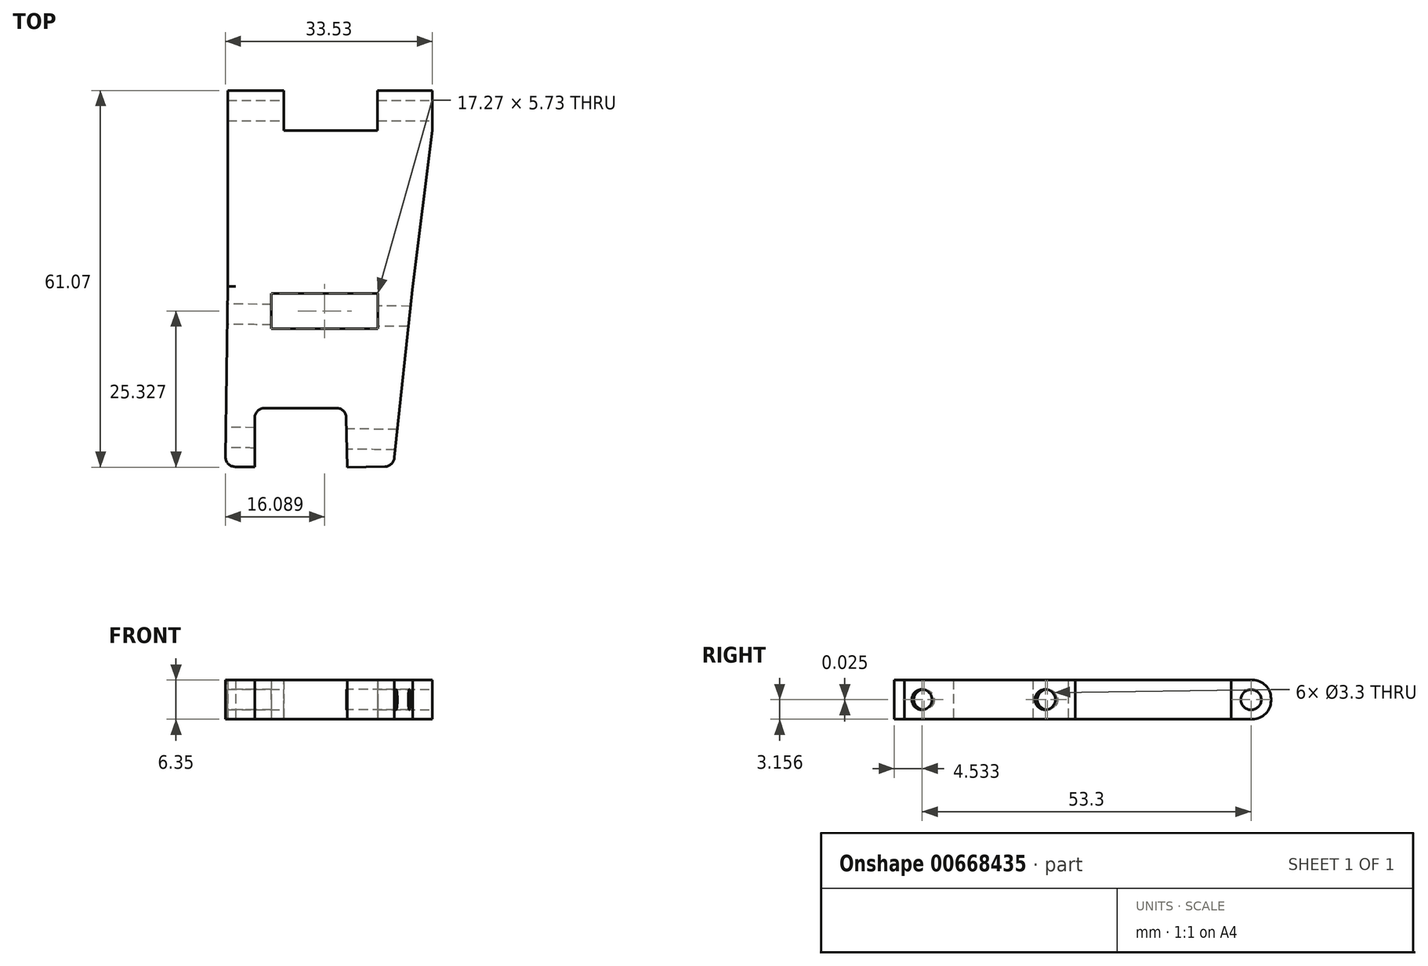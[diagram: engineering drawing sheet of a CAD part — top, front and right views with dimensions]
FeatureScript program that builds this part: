
annotation { "Feature Type Name" : "Feature", "Feature Type Description" : "" }
export const myFeature = defineFeature(function(context is Context, id is Id, definition is map)
    precondition{}
    {
        {
            var Q0;
            Q0=qCreatedBy(makeId("Top.planeOp"),FACE);
            var sketch = newSketch(context, id + "F0", { "sketchPlane" : qUnion([Q0])});
            skLineSegment(sketch, "E0.bottom", {"start": v(-49.27, 51.46) * mm, "end": v(-40.15, 51.46) * mm});
            skLineSegment(sketch, "E0.top", {"start": v(-49.27, 19.7) * mm, "end": v(-19.3, 19.7) * mm});
            skLineSegment(sketch, "E0.left", {"start": v(-49.27, 51.46) * mm, "end": v(-49.27, 19.7) * mm});
            skLineSegment(sketch, "E0.right", {"start": v(-16.1, 51.46) * mm, "end": v(-16.1, 45.01) * mm});
            skLineSegment(sketch, "E1", {"start": v(-40.15, 51.46) * mm, "end": v(-40.15, 45.01) * mm});
            skLineSegment(sketch, "E2", {"start": v(-40.15, 45.01) * mm, "end": v(-25, 45.01) * mm});
            skLineSegment(sketch, "E3", {"start": v(-25, 45.01) * mm, "end": v(-25, 51.46) * mm});
            skLineSegment(sketch, "E4", {"start": v(-25, 51.46) * mm, "end": v(-16.1, 51.46) * mm});
            skLineSegment(sketch, "E5", {"start": v(-16.1, 45.01) * mm, "end": v(-19.3, 19.7) * mm});
            skSolve(sketch);
        }
        {
            var Q0;
            Q0=makeQuery(id+"F0.imprint","IMPRINT",FACE,{"disambiguationData":[TD([[makeQuery(id+"F0.imprint","IMPRINT",EDGE,{"derivedFrom":sQuery(id+"F0.wireOp",EDGE,"E0.top")}),1.0]])]});
            extrude(context, id + "F1", {"entities" : qUnion([Q0]), "depth" : 6.35 * mm});
        }
        {
            var Q0;
            Q0=makeQuery(id+"F1.opExtrude","SWEPT_FACE",FACE,{"disambiguationData":[OSD([sQuery(id+"F0.wireOp",EDGE,"E0.right")])]});
            var sketch = newSketch(context, id + "F2", { "sketchPlane" : qUnion([Q0])});
            skCircle(sketch, "E6", {"center": v(48.22, 3.16) * mm, "radius": 1.5 * mm});
            skSolve(sketch);
        }
        {
            var Q0;
            Q0=sQuery(id+"F2.wireOp",VERTEX,"E6.center");
            var Q1;
            Q1=makeQuery(id+"F1.opExtrude","SWEPT_BODY",BODY,{"disambiguationData":[OSD([sQuery(id+"F0.wireOp",EDGE,"E0.top"),sQuery(id+"F0.wireOp",EDGE,"E0.left"),sQuery(id+"F0.wireOp",EDGE,"E0.bottom"),sQuery(id+"F0.wireOp",EDGE,"E1"),sQuery(id+"F0.wireOp",EDGE,"E2"),sQuery(id+"F0.wireOp",EDGE,"E3"),sQuery(id+"F0.wireOp",EDGE,"E0.right"),sQuery(id+"F0.wireOp",EDGE,"E5"),sQuery(id+"F0.wireOp",EDGE,"E4")])]});
            hole(context, id + "F3", {"style" : HoleStyle.SIMPLE, "endStyle" : HoleEndStyle.THROUGH, "standardTappedOrClearance" : lookupTablePath({ "standard" : "ISO", "fit" : "Normal", "size" : "M3", "type" : "Clearance" }), "standardBlindInLast" : lookupTablePath({ "fit" : "Standard", "standard" : "ISO", "size" : "M3", "type" : "Clearance" }), "holeDiameter" : 3.3 * mm, "isTappedThrough" : true, "tappedDepth" : 12.7 * mm, "tapClearance" : 3, "locations" : qUnion([Q0]), "scope" : qUnion([Q1])});
        }
        {
            var Q0;
            Q0=makeQuery(id+"F1.opExtrude","CAP_EDGE",EDGE,{"disambiguationData":[OSD([sQuery(id+"F0.wireOp",EDGE,"E4")])],"isStart":true});
            var Q1;
            Q1=makeQuery(id+"F1.opExtrude","CAP_EDGE",EDGE,{"disambiguationData":[OSD([sQuery(id+"F0.wireOp",EDGE,"E4")])],"isStart":false});
            var Q2;
            Q2=makeQuery(id+"F1.opExtrude","CAP_EDGE",EDGE,{"disambiguationData":[OSD([sQuery(id+"F0.wireOp",EDGE,"E0.bottom")])],"isStart":true});
            var Q3;
            Q3=makeQuery(id+"F1.opExtrude","CAP_EDGE",EDGE,{"disambiguationData":[OSD([sQuery(id+"F0.wireOp",EDGE,"E0.bottom")])],"isStart":false});
            fillet(context, id + "F4", {"entities" : qUnion([Q0, Q1, Q2, Q3]), "radius" : 3 * mm, "tangentPropagation" : true, "allowEdgeOverflow" : false});
        }
        {
            var Q0;
            Q0=qCreatedBy(makeId("Top.planeOp"),FACE);
            var sketch = newSketch(context, id + "F5", { "sketchPlane" : qUnion([Q0])});
            skLineSegment(sketch, "E7", {"start": v(-49.63, 0) * mm, "end": v(-49.63, -7.95) * mm});
            skLineSegment(sketch, "E8", {"start": v(-44.88, -9.53) * mm, "end": v(-44.88, -1.59) * mm});
            skLineSegment(sketch, "E9", {"start": v(-48.05, -9.53) * mm, "end": v(-44.88, -9.53) * mm});
            skLineSegment(sketch, "E10", {"start": v(-29.9, -9.61) * mm, "end": v(-23.8, -9.5) * mm});
            skLineSegment(sketch, "E11", {"start": v(-43.29, 0) * mm, "end": v(-31.63, 0) * mm});
            skPoint(sketch, "E12.visualSharp", {"position": v(-26.3, 0) * mm});
            skPoint(sketch, "E13.visualSharp", {"position": v(-44.88, 0) * mm});
            skArc(sketch, "E13.filletArc", {"start": v(-43.29, 0) * mm, "mid": v(-44.41, -0.46) * mm, "end": v(-44.88, -1.59) * mm});
            skPoint(sketch, "E14.visualSharp", {"position": v(-49.63, -9.53) * mm});
            skArc(sketch, "E14.filletArc", {"start": v(-49.63, -7.95) * mm, "mid": v(-49.16, -9.06) * mm, "end": v(-48.05, -9.53) * mm});
            skPoint(sketch, "E15.visualSharp", {"position": v(-25.16, -9.53) * mm});
            skArc(sketch, "E15.filletArc", {"start": v(-23.8, -9.5) * mm, "mid": v(-22.7, -9.04) * mm, "end": v(-22.25, -7.95) * mm});
            skLineSegment(sketch, "E16", {"start": v(-19.3, 19.74) * mm, "end": v(-22.25, -7.95) * mm});
            skLineSegment(sketch, "E17", {"start": v(-19.3, 19.74) * mm, "end": v(-49.27, 19.7) * mm});
            skLineSegment(sketch, "E18", {"start": v(-49.27, 19.7) * mm, "end": v(-49.63, -7.95) * mm});
            skLineSegment(sketch, "E19", {"start": v(-29.9, -9.61) * mm, "end": v(-30.05, -1.55) * mm});
            skPoint(sketch, "E20.visualSharp", {"position": v(-30.08, 0) * mm});
            skArc(sketch, "E20.filletArc", {"start": v(-30.05, -1.55) * mm, "mid": v(-30.53, -0.45) * mm, "end": v(-31.63, 0) * mm});
            skLineSegment(sketch, "E21.bottom", {"start": v(-42.17, 18.58) * mm, "end": v(-24.9, 18.58) * mm});
            skLineSegment(sketch, "E21.top", {"start": v(-42.17, 12.85) * mm, "end": v(-24.9, 12.85) * mm});
            skLineSegment(sketch, "E21.left", {"start": v(-42.17, 18.58) * mm, "end": v(-42.17, 12.85) * mm});
            skLineSegment(sketch, "E21.right", {"start": v(-24.9, 18.58) * mm, "end": v(-24.9, 12.85) * mm});
            skSolve(sketch);
        }
        {
            var Q0;
            Q0=makeQuery(id+"F5.imprint","IMPRINT",FACE,{"disambiguationData":[TD([[makeQuery(id+"F5.imprint","IMPRINT",EDGE,{"derivedFrom":sQuery(id+"F5.wireOp",EDGE,"E8")}),1.0]])]});
            extrude(context, id + "F6", {"entities" : qUnion([Q0]), "operationType" : NewBodyOperationType.ADD, "depth" : 6.35 * mm});
        }
        {
            var Q0;
            Q0=makeQuery(id+"F6.opExtrude","SWEPT_FACE",FACE,{"disambiguationData":[OSD([sQuery(id+"F5.wireOp",EDGE,"E18")])]});
            var sketch = newSketch(context, id + "F7", { "sketchPlane" : qUnion([Q0])});
            skCircle(sketch, "E22", {"center": v(5.4, 3.18) * mm, "radius": 1.5 * mm});
            skPoint(sketch, "E23.start.orphan", {"position": v(8.58, 0) * mm});
            skPoint(sketch, "E24.start.orphan", {"position": v(2.23, 6.35) * mm});
            skSolve(sketch);
        }
        {
            var Q0;
            Q0=sQuery(id+"F7.wireOp",VERTEX,"E22.center");
            var Q1;
            Q1=makeQuery(id+"F1.opExtrude","SWEPT_BODY",BODY,{"disambiguationData":[OSD([sQuery(id+"F0.wireOp",EDGE,"E0.top"),sQuery(id+"F0.wireOp",EDGE,"E0.left"),sQuery(id+"F0.wireOp",EDGE,"E0.bottom"),sQuery(id+"F0.wireOp",EDGE,"E1"),sQuery(id+"F0.wireOp",EDGE,"E2"),sQuery(id+"F0.wireOp",EDGE,"E3"),sQuery(id+"F0.wireOp",EDGE,"E0.right"),sQuery(id+"F0.wireOp",EDGE,"E5"),sQuery(id+"F0.wireOp",EDGE,"E4")])]});
            hole(context, id + "F8", {"style" : HoleStyle.SIMPLE, "endStyle" : HoleEndStyle.THROUGH, "standardTappedOrClearance" : lookupTablePath({ "standard" : "ISO", "fit" : "Normal", "size" : "M3", "type" : "Clearance" }), "standardBlindInLast" : lookupTablePath({ "fit" : "Standard", "standard" : "ISO", "size" : "M3", "type" : "Clearance" }), "holeDiameter" : 3.3 * mm, "isTappedThrough" : true, "tappedDepth" : 12.7 * mm, "tapClearance" : 3, "locations" : qUnion([Q0]), "scope" : qUnion([Q1])});
        }
        {
            var Q0;
            Q0=makeQuery(id+"F6.opExtrude","SWEPT_FACE",FACE,{"disambiguationData":[OSD([sQuery(id+"F5.wireOp",EDGE,"E18")])]});
            var sketch = newSketch(context, id + "F9", { "sketchPlane" : qUnion([Q0])});
            skCircle(sketch, "E25", {"center": v(-14.6, 3.18) * mm, "radius": 2 * mm});
            skSolve(sketch);
        }
        {
            var Q0;
            Q0=sQuery(id+"F9.wireOp",VERTEX,"E25.center");
            var Q1;
            Q1=makeQuery(id+"F1.opExtrude","SWEPT_BODY",BODY,{"disambiguationData":[OSD([sQuery(id+"F0.wireOp",EDGE,"E0.top"),sQuery(id+"F0.wireOp",EDGE,"E0.left"),sQuery(id+"F0.wireOp",EDGE,"E0.bottom"),sQuery(id+"F0.wireOp",EDGE,"E1"),sQuery(id+"F0.wireOp",EDGE,"E2"),sQuery(id+"F0.wireOp",EDGE,"E3"),sQuery(id+"F0.wireOp",EDGE,"E0.right"),sQuery(id+"F0.wireOp",EDGE,"E5"),sQuery(id+"F0.wireOp",EDGE,"E4")])]});
            hole(context, id + "F10", {"style" : HoleStyle.SIMPLE, "endStyle" : HoleEndStyle.THROUGH, "standardTappedOrClearance" : lookupTablePath({ "standard" : "ISO", "fit" : "Normal", "size" : "M3", "type" : "Clearance" }), "standardBlindInLast" : lookupTablePath({ "fit" : "Standard", "standard" : "ISO", "size" : "M3", "type" : "Clearance" }), "holeDiameter" : 3.3 * mm, "isTappedThrough" : true, "tappedDepth" : 12.7 * mm, "tapClearance" : 3, "locations" : qUnion([Q0]), "scope" : qUnion([Q1])});
        }
    });
